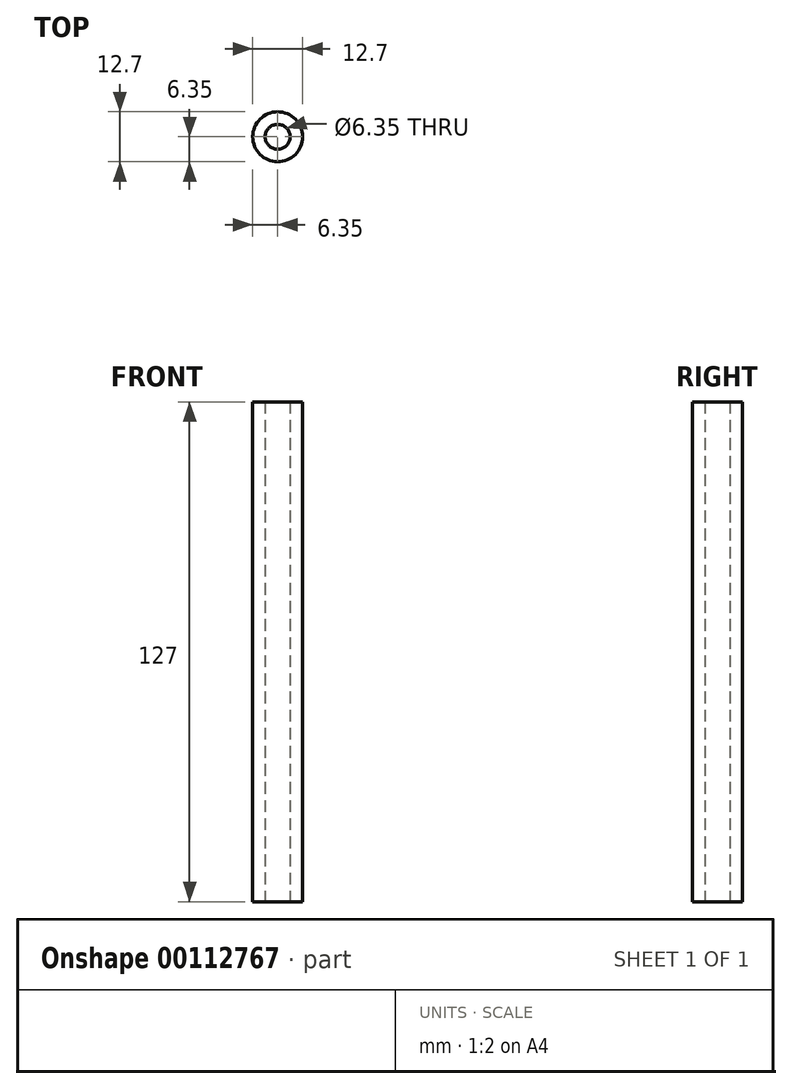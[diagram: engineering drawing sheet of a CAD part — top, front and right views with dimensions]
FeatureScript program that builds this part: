
annotation { "Feature Type Name" : "Feature", "Feature Type Description" : "" }
export const myFeature = defineFeature(function(context is Context, id is Id, definition is map)
    precondition{}
    {
        {
            var Q0;
            Q0=qCreatedBy(makeId("Top.planeOp"),FACE);
            var sketch = newSketch(context, id + "F0", { "sketchPlane" : qUnion([Q0])});
            skCircle(sketch, "E0", {"center": v(0, 0) * mm, "radius": 3.18 * mm});
            skCircle(sketch, "E1", {"center": v(0, 0) * mm, "radius": 6.35 * mm});
            skSolve(sketch);
        }
        {
            var Q0;
            Q0=makeQuery(id+"F0.imprint","IMPRINT",FACE,{"disambiguationData":[TD([[makeQuery(id+"F0.imprint","IMPRINT",EDGE,{"derivedFrom":sQuery(id+"F0.wireOp",EDGE,"E0")}),-1.0]])]});
            extrude(context, id + "F1", {"entities" : qUnion([Q0]), "depth" : 127 * mm});
        }
    });
